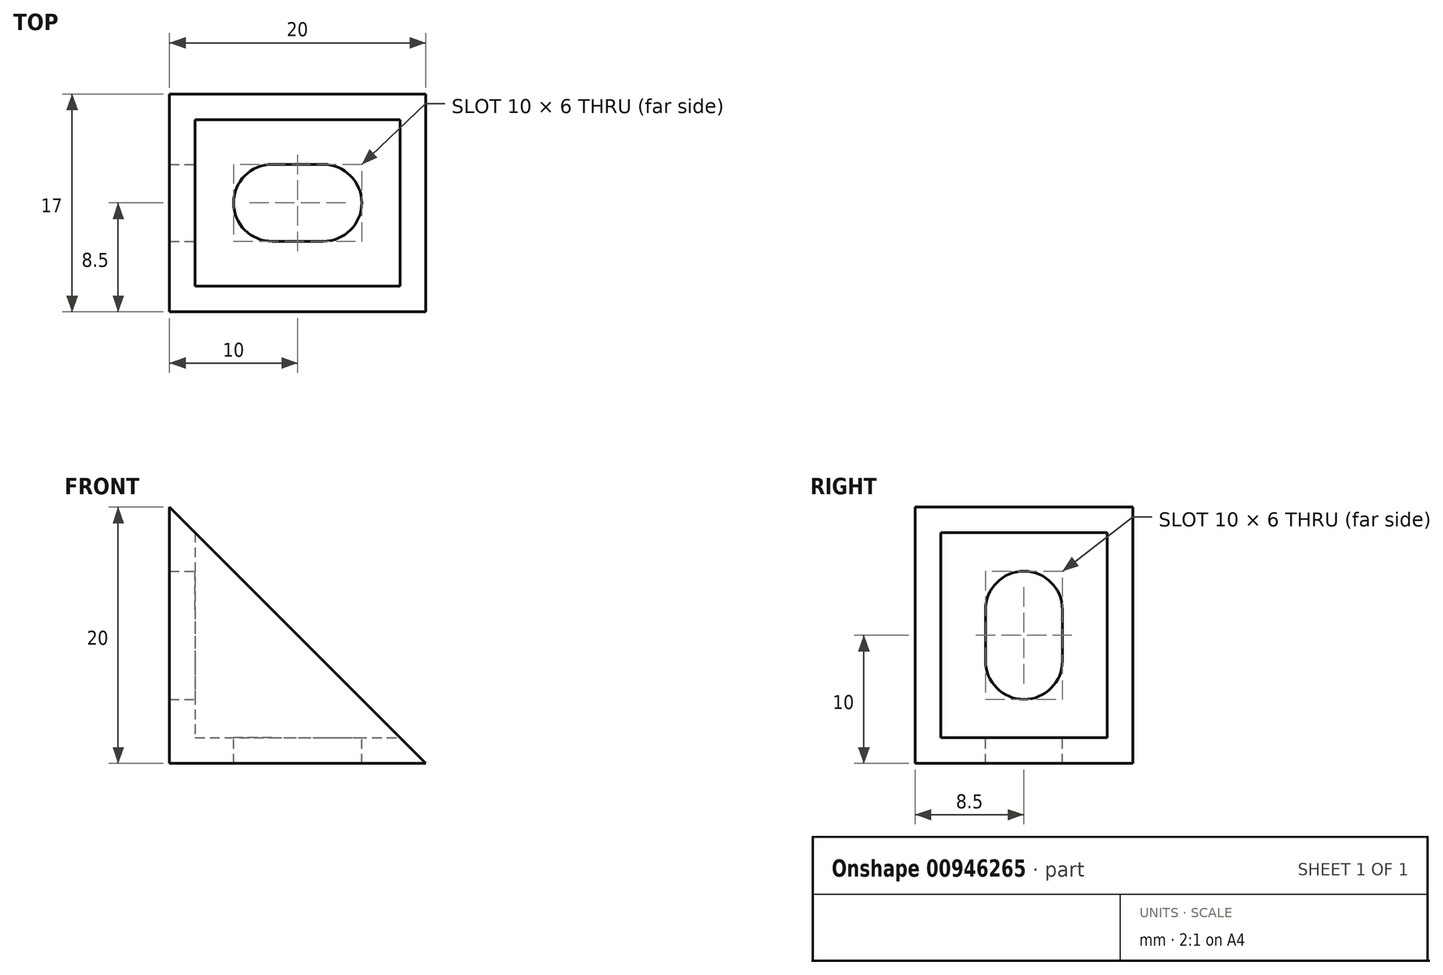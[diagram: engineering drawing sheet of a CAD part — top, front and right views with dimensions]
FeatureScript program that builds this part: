
annotation { "Feature Type Name" : "Feature", "Feature Type Description" : "" }
export const myFeature = defineFeature(function(context is Context, id is Id, definition is map)
    precondition{}
    {
        {
            var Q0;
            Q0=qCreatedBy(makeId("Front.planeOp"),FACE);
            var sketch = newSketch(context, id + "F0", { "sketchPlane" : qUnion([Q0])});
            skLineSegment(sketch, "E0", {"start": v(0, 0) * mm, "end": v(0, 20) * mm});
            skLineSegment(sketch, "E1", {"start": v(0, 20) * mm, "end": v(20, 0) * mm});
            skLineSegment(sketch, "E2", {"start": v(20, 0) * mm, "end": v(0, 0) * mm});
            skLineSegment(sketch, "E3.0", {"start": v(2, 2) * mm, "end": v(2, 18) * mm});
            skLineSegment(sketch, "E3.1", {"start": v(18, 2) * mm, "end": v(2, 2) * mm});
            skSolve(sketch);
        }
        {
            var Q0;
            Q0 = qSketchRegion(id + "F0", true);
            extrude(context, id + "F1", {"entities" : qUnion([Q0]), "oppositeDirection" : true, "depth" : 17 * mm, "offsetDistance" : 25 * mm});
        }
        {
            var Q0;
            {var subQ0=sQuery(id+"F0.wireOp",EDGE,"E3.0");Q0=makeQuery(id+"F0.imprint","IMPRINT",FACE,{"disambiguationData":[TD([[makeQuery(id+"F0.imprint","IMPRINT",EDGE,{"derivedFrom":subQ0}),-1.0]])]});}
            cPlane(context, id + "F2", {"entities" : qUnion([Q0]), "cplaneType" : CPlaneType.OFFSET, "offset" : 2 * mm, "oppositeDirection" : true, "width" : 150 * mm, "height" : 150 * mm});
        }
        {
            var Q0;
            Q0=qCreatedBy(id+"F2.planeOp",FACE);
            var sketch = newSketch(context, id + "F3", { "sketchPlane" : qUnion([Q0])});
            skLineSegment(sketch, "E4.0.0", {"start": v(18, 2) * mm, "end": v(2, 18) * mm});
            skLineSegment(sketch, "E4.0.1", {"start": v(2, 18) * mm, "end": v(2, 2) * mm});
            skLineSegment(sketch, "E4.0.2", {"start": v(2, 2) * mm, "end": v(18, 2) * mm});
            skSolve(sketch);
        }
        {
            var Q0;
            Q0 = qSketchRegion(id + "F3", true);
            extrude(context, id + "F4", {"entities" : qUnion([Q0]), "operationType" : NewBodyOperationType.REMOVE, "oppositeDirection" : true, "depth" : 13 * mm, "offsetDistance" : 25 * mm});
        }
        {
            var Q0;
            Q0=makeQuery(id+"F4.boolean.opBoolean","COPY",FACE,{"derivedFrom":makeQuery(id+"F4.opExtrude","SWEPT_FACE",FACE,{"disambiguationData":[OSD([sQuery(id+"F3.wireOp",EDGE,"E4.0.1")])]})});
            var sketch = newSketch(context, id + "F5", { "sketchPlane" : qUnion([Q0])});
            skLineSegment(sketch, "E5", {"start": v(8.5, 12) * mm, "end": v(8.5, 8) * mm});
            skArc(sketch, "E6.0.startCap", {"start": v(5.5, 12) * mm, "mid": v(8.5, 15) * mm, "end": v(11.5, 12) * mm});
            skArc(sketch, "E6.0.endCap", {"start": v(11.5, 8) * mm, "mid": v(8.5, 5) * mm, "end": v(5.5, 8) * mm});
            skLineSegment(sketch, "E6.0.left", {"start": v(11.5, 12) * mm, "end": v(11.5, 8) * mm});
            skLineSegment(sketch, "E6.0.right", {"start": v(5.5, 12) * mm, "end": v(5.5, 8) * mm});
            skSolve(sketch);
        }
        {
            var Q0;
            Q0 = qSketchRegion(id + "F5", true);
            extrude(context, id + "F6", {"entities" : qUnion([Q0]), "operationType" : NewBodyOperationType.REMOVE, "endBound" : BoundingType.THROUGH_ALL, "oppositeDirection" : true, "depth" : 25 * mm, "offsetDistance" : 25 * mm});
        }
        {
            var Q0;
            Q0=makeQuery(id+"F4.boolean.opBoolean","COPY",FACE,{"derivedFrom":makeQuery(id+"F4.opExtrude","SWEPT_FACE",FACE,{"disambiguationData":[OSD([sQuery(id+"F3.wireOp",EDGE,"E4.0.2")])]})});
            var sketch = newSketch(context, id + "F7", { "sketchPlane" : qUnion([Q0])});
            skLineSegment(sketch, "E7", {"start": v(8, 8.5) * mm, "end": v(12, 8.5) * mm});
            skArc(sketch, "E8.0.startCap", {"start": v(8, 5.5) * mm, "mid": v(5, 8.5) * mm, "end": v(8, 11.5) * mm});
            skArc(sketch, "E8.0.endCap", {"start": v(12, 11.5) * mm, "mid": v(15, 8.5) * mm, "end": v(12, 5.5) * mm});
            skLineSegment(sketch, "E8.0.left", {"start": v(8, 11.5) * mm, "end": v(12, 11.5) * mm});
            skLineSegment(sketch, "E8.0.right", {"start": v(8, 5.5) * mm, "end": v(12, 5.5) * mm});
            skSolve(sketch);
        }
        {
            var Q0;
            Q0 = qSketchRegion(id + "F7", true);
            extrude(context, id + "F8", {"entities" : qUnion([Q0]), "operationType" : NewBodyOperationType.REMOVE, "endBound" : BoundingType.THROUGH_ALL, "oppositeDirection" : true, "depth" : 25 * mm, "offsetDistance" : 25 * mm});
        }
    });
